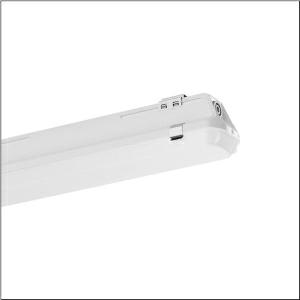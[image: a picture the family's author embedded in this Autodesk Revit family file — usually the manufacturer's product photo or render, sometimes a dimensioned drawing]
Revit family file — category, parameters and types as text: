
# Revit family: monsun_r__21_51fb20dl447j3h_de49
name_source: partatom
category: Lighting Fixtures
units: mm (PartAtom-declared; Revit-internal decimal feet)

## family parameters
Cut with Voids When Loaded = No
Host = Face
Light Source = No
Part Type = Normal
Room Calculation Point = No
Round Connector Dimension = Use Diameter
Shared = No

## types (1)
- --- (1 x LED, 760 lm, 4.5 W, 4000K)
    Apparent Load = 5 VA
    CIE Flux Codes = 45 75 93 94 100
    Color Rendering = 80
    Color Temperature = 4000K
    Default Elevation = 1800 mm
    Description = Monsun® 21, damp-proof luminaire, chain hanger, primary optical cover: enclosure, of PC, light emission: direct distribution, primary light characteristic: symmetric, installation type: suspended mounting, surface-mounted, horizontal mounting, vertical mounting, LED, rated luminous flux: 4.320lm, luminous efficacy: 127lm/W, light colour: 840, colour temperature: 4000K, control gear: ECG DALI, with terminal, 5-pole, max. 2.5mm², mains connection: 220..240V, AC, 50/60Hz, rated input power: 34W, control gear: single battery element, battery: NiCd, 4,5Ah, mains connection: 230V, housing, of glass-fibre reinforced plastic, uncoated, bright grey, incl. chain hanger, length: 1.299mm, width: 90mm, height: 88mm, clip for enclosure, of stainless steel (V2A), ceiling mounting element, of stainless steel (V2A), chain hanger, of stainless steel (V2A), protection rating (complete): IP66, insulation class (complete): insulation class I (protective earthing), certification: CE, UKCA, protection symbol: D, impact resistance: IK08, permissible operating ambient temperature: +5..+25°C, standard: EN 50419, EN 60598-2-1, corresponds to IFS (International Featured Standards) requirements for safety and quality in the food industry, for indoor or canopied outdoor use, no direct snow, no direct sun, no direct rain, contact your sales advisor before using the luminaires in applications with unclear chemical exposure, large temperature fluctuations or condensation-forming humidity, LABS conformity tested according to VDMA 24364:2018-05, packaging unit: 1 piece
    Height = 88 mm
    Lamp = 1 x LED
    Lamp Light Flux = 760 lm
    Lamp Power = 4.5 W
    Lamp count = 1
    Length = 1299 mm
    Luminous efficacy = 169 lm/W
    Manufacturer = Siteco
    ModVariant = No
    Model = 51FB20DL447J3H
    Mounting Place = Ceiling
    Mounting Type = Surface mounted
    Number of Poles = 1
    OnlyDefault = Yes
    Power Factor = 1
    Product Name = Monsun® 21
    Product group = damp-proof luminaire
    ProductGroupID = 300
    Protection Class = Protection class I
    Protection Degree = IP 66
    RLX_Detail_Level = 1
    RLX_Emergency_Light_Flux = 0 lm
    RLX_Emergency_Type = 0
    RLX_Emergency_Type_DB = No
    RlxData = <blob elided: 93557 chars, md5=fb80032e>
    Socket = socket
    Standby Power = 0 W
    System Light Flux = 760 lm
    System Power = 5 W
    Type Comments = : 3 h
    Type Image = l_1006717.jpg
    URL = http://relux.com
    VarID = @adj_074837
    Voltage = 0 V
    Weight = 0.00 kg
    Width = 90 mm

## geometry (parser evidence)
native form markers: Blend x4, Sweep x13
no freeform markers — native parametric forms only
